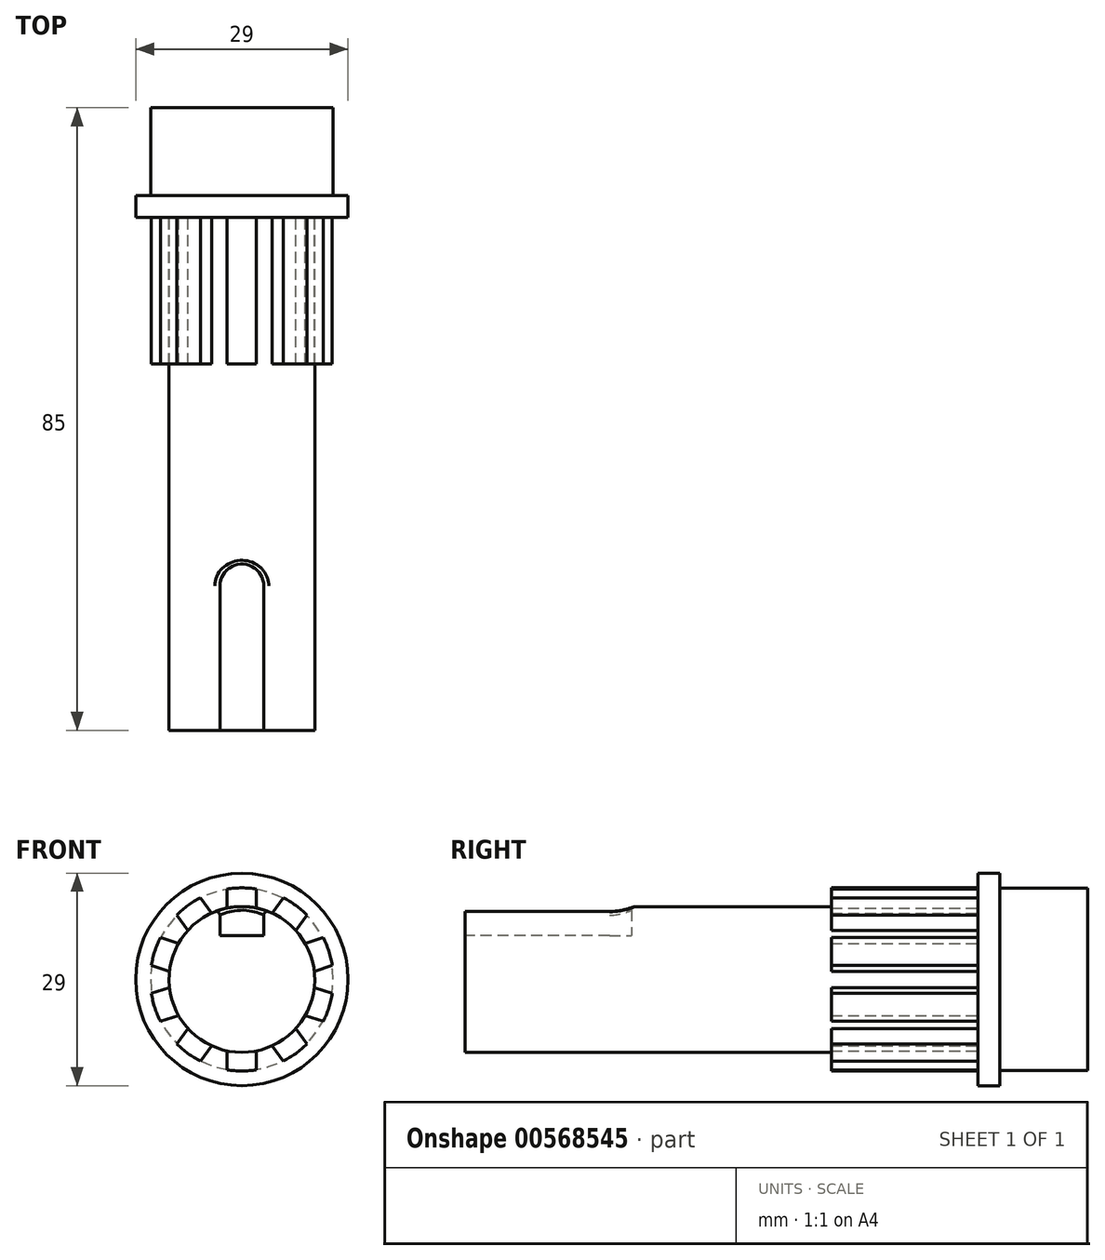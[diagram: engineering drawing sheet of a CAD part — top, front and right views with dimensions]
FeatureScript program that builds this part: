
annotation { "Feature Type Name" : "Feature", "Feature Type Description" : "" }
export const myFeature = defineFeature(function(context is Context, id is Id, definition is map)
    precondition{}
    {
        {
            var Q0;
            Q0=qCreatedBy(makeId("Front.planeOp"),FACE);
            var sketch = newSketch(context, id + "F0", { "sketchPlane" : qUnion([Q0])});
            skCircle(sketch, "E0", {"center": v(0, 0) * mm, "radius": 12.45 * mm});
            skSolve(sketch);
        }
        {
            var Q0;
            Q0 = qSketchRegion(id + "F0", true);
            extrude(context, id + "F1", {"entities" : qUnion([Q0]), "oppositeDirection" : true, "depth" : 12 * mm, "offsetDistance" : 25 * mm});
        }
        {
            var Q0;
            Q0=qCreatedBy(makeId("Front.planeOp"),FACE);
            var sketch = newSketch(context, id + "F2", { "sketchPlane" : qUnion([Q0])});
            skCircle(sketch, "E1", {"center": v(0, 0) * mm, "radius": 14.5 * mm});
            skSolve(sketch);
        }
        {
            var Q0;
            Q0 = qSketchRegion(id + "F2", true);
            extrude(context, id + "F3", {"entities" : qUnion([Q0]), "operationType" : NewBodyOperationType.ADD, "depth" : 3 * mm, "offsetDistance" : 25 * mm});
        }
        {
            var Q0;
            Q0=makeQuery(id+"F3.opExtrude","CAP_FACE",FACE,{"disambiguationData":[OSD([sQuery(id+"F2.wireOp",EDGE,"E1")])],"isStart":false});
            var sketch = newSketch(context, id + "F4", { "sketchPlane" : qUnion([Q0])});
            skCircle(sketch, "E2", {"center": v(0, 0) * mm, "radius": 9.95 * mm});
            skSolve(sketch);
        }
        {
            var Q0;
            Q0 = qSketchRegion(id + "F4", true);
            extrude(context, id + "F5", {"entities" : qUnion([Q0]), "operationType" : NewBodyOperationType.ADD, "depth" : 70 * mm, "offsetDistance" : 25 * mm});
        }
        {
            var Q0;
            Q0=makeQuery(id+"F3.opExtrude","CAP_FACE",FACE,{"disambiguationData":[OSD([sQuery(id+"F2.wireOp",EDGE,"E1")])],"isStart":false});
            var sketch = newSketch(context, id + "F6", { "sketchPlane" : qUnion([Q0])});
            skArc(sketch, "E3", {"start": v(2, 12.34) * mm, "mid": v(0, 12.5) * mm, "end": v(-2, 12.34) * mm});
            skLineSegment(sketch, "E4", {"start": v(-2, 12.34) * mm, "end": v(-2, 5.62) * mm});
            skLineSegment(sketch, "E5", {"start": v(-2, 5.62) * mm, "end": v(2, 5.62) * mm});
            skLineSegment(sketch, "E6", {"start": v(2, 5.62) * mm, "end": v(2, 12.34) * mm});
            skPoint(sketch, "E7.orphan", {"position": v(2, 18.42) * mm});
            skLineSegment(sketch, "E8.1.0", {"start": v(-8.87, 8.8) * mm, "end": v(-4.92, 3.37) * mm});
            skArc(sketch, "E8.1.1", {"start": v(-5.63, 11.16) * mm, "mid": v(-7.35, 10.11) * mm, "end": v(-8.87, 8.8) * mm});
            skLineSegment(sketch, "E8.1.2", {"start": v(-1.69, 5.72) * mm, "end": v(-5.63, 11.16) * mm});
            skLineSegment(sketch, "E8.1.3", {"start": v(-4.92, 3.37) * mm, "end": v(-1.69, 5.72) * mm});
            skLineSegment(sketch, "E8.2.0", {"start": v(-12.35, 1.91) * mm, "end": v(-5.96, -0.17) * mm});
            skArc(sketch, "E8.2.1", {"start": v(-11.12, 5.72) * mm, "mid": v(-11.89, 3.86) * mm, "end": v(-12.35, 1.91) * mm});
            skLineSegment(sketch, "E8.2.2", {"start": v(-4.73, 3.64) * mm, "end": v(-11.12, 5.72) * mm});
            skLineSegment(sketch, "E8.2.3", {"start": v(-5.96, -0.17) * mm, "end": v(-4.73, 3.64) * mm});
            skLineSegment(sketch, "E8.3.0", {"start": v(-11.12, -5.72) * mm, "end": v(-4.73, -3.64) * mm});
            skArc(sketch, "E8.3.1", {"start": v(-12.35, -1.91) * mm, "mid": v(-11.89, -3.86) * mm, "end": v(-11.12, -5.72) * mm});
            skLineSegment(sketch, "E8.3.2", {"start": v(-5.96, 0.17) * mm, "end": v(-12.35, -1.91) * mm});
            skLineSegment(sketch, "E8.3.3", {"start": v(-4.73, -3.64) * mm, "end": v(-5.96, 0.17) * mm});
            skLineSegment(sketch, "E8.4.0", {"start": v(-5.63, -11.16) * mm, "end": v(-1.69, -5.72) * mm});
            skArc(sketch, "E8.4.1", {"start": v(-8.87, -8.8) * mm, "mid": v(-7.35, -10.11) * mm, "end": v(-5.63, -11.16) * mm});
            skLineSegment(sketch, "E8.4.2", {"start": v(-4.92, -3.37) * mm, "end": v(-8.87, -8.8) * mm});
            skLineSegment(sketch, "E8.4.3", {"start": v(-1.69, -5.72) * mm, "end": v(-4.92, -3.37) * mm});
            skLineSegment(sketch, "E8.5.0", {"start": v(2, -12.34) * mm, "end": v(2, -5.62) * mm});
            skArc(sketch, "E8.5.1", {"start": v(-2, -12.34) * mm, "mid": v(0, -12.5) * mm, "end": v(2, -12.34) * mm});
            skLineSegment(sketch, "E8.5.2", {"start": v(-2, -5.62) * mm, "end": v(-2, -12.34) * mm});
            skLineSegment(sketch, "E8.5.3", {"start": v(2, -5.62) * mm, "end": v(-2, -5.62) * mm});
            skLineSegment(sketch, "E8.6.0", {"start": v(8.87, -8.8) * mm, "end": v(4.92, -3.37) * mm});
            skArc(sketch, "E8.6.1", {"start": v(5.63, -11.16) * mm, "mid": v(7.35, -10.11) * mm, "end": v(8.87, -8.8) * mm});
            skLineSegment(sketch, "E8.6.2", {"start": v(1.69, -5.72) * mm, "end": v(5.63, -11.16) * mm});
            skLineSegment(sketch, "E8.6.3", {"start": v(4.92, -3.37) * mm, "end": v(1.69, -5.72) * mm});
            skLineSegment(sketch, "E8.7.0", {"start": v(12.35, -1.91) * mm, "end": v(5.96, 0.17) * mm});
            skArc(sketch, "E8.7.1", {"start": v(11.12, -5.72) * mm, "mid": v(11.89, -3.86) * mm, "end": v(12.35, -1.91) * mm});
            skLineSegment(sketch, "E8.7.2", {"start": v(4.73, -3.64) * mm, "end": v(11.12, -5.72) * mm});
            skLineSegment(sketch, "E8.7.3", {"start": v(5.96, 0.17) * mm, "end": v(4.73, -3.64) * mm});
            skLineSegment(sketch, "E8.8.0", {"start": v(11.12, 5.72) * mm, "end": v(4.73, 3.64) * mm});
            skArc(sketch, "E8.8.1", {"start": v(12.35, 1.91) * mm, "mid": v(11.89, 3.86) * mm, "end": v(11.12, 5.72) * mm});
            skLineSegment(sketch, "E8.8.2", {"start": v(5.96, -0.17) * mm, "end": v(12.35, 1.91) * mm});
            skLineSegment(sketch, "E8.8.3", {"start": v(4.73, 3.64) * mm, "end": v(5.96, -0.17) * mm});
            skLineSegment(sketch, "E8.9.0", {"start": v(5.63, 11.16) * mm, "end": v(1.69, 5.72) * mm});
            skArc(sketch, "E8.9.1", {"start": v(8.87, 8.8) * mm, "mid": v(7.35, 10.11) * mm, "end": v(5.63, 11.16) * mm});
            skLineSegment(sketch, "E8.9.2", {"start": v(4.92, 3.37) * mm, "end": v(8.87, 8.8) * mm});
            skLineSegment(sketch, "E8.9.3", {"start": v(1.69, 5.72) * mm, "end": v(4.92, 3.37) * mm});
            skSolve(sketch);
        }
        {
            var Q0;
            {var subQ0=sQuery(id+"F6.wireOp",EDGE,"E3");Q0=makeQuery(id+"F6.imprint","IMPRINT",FACE,{"disambiguationData":[TD([[makeQuery(id+"F6.imprint","IMPRINT",EDGE,{"derivedFrom":subQ0}),1.0]])]});}
            var Q1;
            {var subQ0=sQuery(id+"F6.wireOp",EDGE,"E8.9.1");Q1=makeQuery(id+"F6.imprint","IMPRINT",FACE,{"disambiguationData":[TD([[makeQuery(id+"F6.imprint","IMPRINT",EDGE,{"derivedFrom":subQ0}),1.0]])]});}
            var Q2;
            {var subQ0=sQuery(id+"F6.wireOp",EDGE,"E8.8.1");Q2=makeQuery(id+"F6.imprint","IMPRINT",FACE,{"disambiguationData":[TD([[makeQuery(id+"F6.imprint","IMPRINT",EDGE,{"derivedFrom":subQ0}),1.0]])]});}
            var Q3;
            {var subQ0=sQuery(id+"F6.wireOp",EDGE,"E8.7.1");Q3=makeQuery(id+"F6.imprint","IMPRINT",FACE,{"disambiguationData":[TD([[makeQuery(id+"F6.imprint","IMPRINT",EDGE,{"derivedFrom":subQ0}),1.0]])]});}
            var Q4;
            {var subQ0=sQuery(id+"F6.wireOp",EDGE,"E8.6.1");Q4=makeQuery(id+"F6.imprint","IMPRINT",FACE,{"disambiguationData":[TD([[makeQuery(id+"F6.imprint","IMPRINT",EDGE,{"derivedFrom":subQ0}),1.0]])]});}
            var Q5;
            {var subQ0=sQuery(id+"F6.wireOp",EDGE,"E8.5.1");Q5=makeQuery(id+"F6.imprint","IMPRINT",FACE,{"disambiguationData":[TD([[makeQuery(id+"F6.imprint","IMPRINT",EDGE,{"derivedFrom":subQ0}),1.0]])]});}
            var Q6;
            {var subQ0=sQuery(id+"F6.wireOp",EDGE,"E8.4.1");Q6=makeQuery(id+"F6.imprint","IMPRINT",FACE,{"disambiguationData":[TD([[makeQuery(id+"F6.imprint","IMPRINT",EDGE,{"derivedFrom":subQ0}),1.0]])]});}
            var Q7;
            {var subQ0=sQuery(id+"F6.wireOp",EDGE,"E8.3.1");Q7=makeQuery(id+"F6.imprint","IMPRINT",FACE,{"disambiguationData":[TD([[makeQuery(id+"F6.imprint","IMPRINT",EDGE,{"derivedFrom":subQ0}),1.0]])]});}
            var Q8;
            {var subQ0=sQuery(id+"F6.wireOp",EDGE,"E8.2.1");Q8=makeQuery(id+"F6.imprint","IMPRINT",FACE,{"disambiguationData":[TD([[makeQuery(id+"F6.imprint","IMPRINT",EDGE,{"derivedFrom":subQ0}),1.0]])]});}
            var Q9;
            {var subQ0=sQuery(id+"F6.wireOp",EDGE,"E8.1.1");Q9=makeQuery(id+"F6.imprint","IMPRINT",FACE,{"disambiguationData":[TD([[makeQuery(id+"F6.imprint","IMPRINT",EDGE,{"derivedFrom":subQ0}),1.0]])]});}
            extrude(context, id + "F7", {"entities" : qUnion([Q0, Q1, Q2, Q3, Q4, Q5, Q6, Q7, Q8, Q9]), "operationType" : NewBodyOperationType.ADD, "depth" : 20 * mm, "offsetDistance" : 25 * mm});
        }
        {
            var Q0;
            Q0=qCreatedBy(makeId("Top.planeOp"),FACE);
            cPlane(context, id + "F8", {"entities" : qUnion([Q0]), "cplaneType" : CPlaneType.OFFSET, "offset" : 6 * mm, "width" : 150 * mm, "height" : 150 * mm});
        }
        {
            var Q0;
            Q0=qCreatedBy(id+"F8.planeOp",FACE);
            var sketch = newSketch(context, id + "F9", { "sketchPlane" : qUnion([Q0])});
            skLineSegment(sketch, "E9.top", {"start": v(-3, -79.7) * mm, "end": v(3, -79.7) * mm});
            skLineSegment(sketch, "E9.left", {"start": v(-3, -53.29) * mm, "end": v(-3, -79.7) * mm});
            skLineSegment(sketch, "E9.right", {"start": v(3, -53.29) * mm, "end": v(3, -79.7) * mm});
            skArc(sketch, "E10", {"start": v(3, -53.29) * mm, "mid": v(0, -50.29) * mm, "end": v(-3, -53.29) * mm});
            skSolve(sketch);
        }
        {
            var Q0;
            Q0=makeQuery(id+"F9.imprint","IMPRINT",FACE,{"disambiguationData":[TD([[makeQuery(id+"F9.imprint","IMPRINT",EDGE,{"derivedFrom":sQuery(id+"F9.wireOp",EDGE,"E9.top")}),1.0]])]});
            extrude(context, id + "F10", {"entities" : qUnion([Q0]), "operationType" : NewBodyOperationType.REMOVE, "depth" : 25 * mm, "offsetDistance" : 25 * mm});
        }
        {
            var Q0;
            Q0=makeQuery(id+"F10.boolean.opBoolean","INTERSECT",EDGE,{"derivedFrom":[makeQuery(id+"F5.opExtrude","SWEPT_FACE",FACE,{"disambiguationData":[OSD([sQuery(id+"F4.wireOp",EDGE,"E2")])]}),makeQuery(id+"F10.opExtrude","SWEPT_FACE",FACE,{"disambiguationData":[OSD([sQuery(id+"F9.wireOp",EDGE,"E9.left")])]})]});
            var Q1;
            Q1=makeQuery(id+"F10.boolean.opBoolean","INTERSECT",EDGE,{"derivedFrom":[makeQuery(id+"F5.opExtrude","SWEPT_FACE",FACE,{"disambiguationData":[OSD([sQuery(id+"F4.wireOp",EDGE,"E2")])]}),makeQuery(id+"F10.opExtrude","SWEPT_FACE",FACE,{"disambiguationData":[OSD([sQuery(id+"F9.wireOp",EDGE,"E9.right")])]})]});
            var Q2;
            Q2=makeQuery(id+"F10.boolean.opBoolean","INTERSECT",EDGE,{"derivedFrom":[makeQuery(id+"F5.opExtrude","SWEPT_FACE",FACE,{"disambiguationData":[OSD([sQuery(id+"F4.wireOp",EDGE,"E2")])]}),makeQuery(id+"F10.opExtrude","SWEPT_FACE",FACE,{"disambiguationData":[OSD([sQuery(id+"F9.wireOp",EDGE,"E10")])]})]});
            fillet(context, id + "F11", {"entities" : qUnion([Q0, Q1, Q2]), "radius" : 0.5 * mm, "tangentPropagation" : true, "allowEdgeOverflow" : false});
        }
    });
